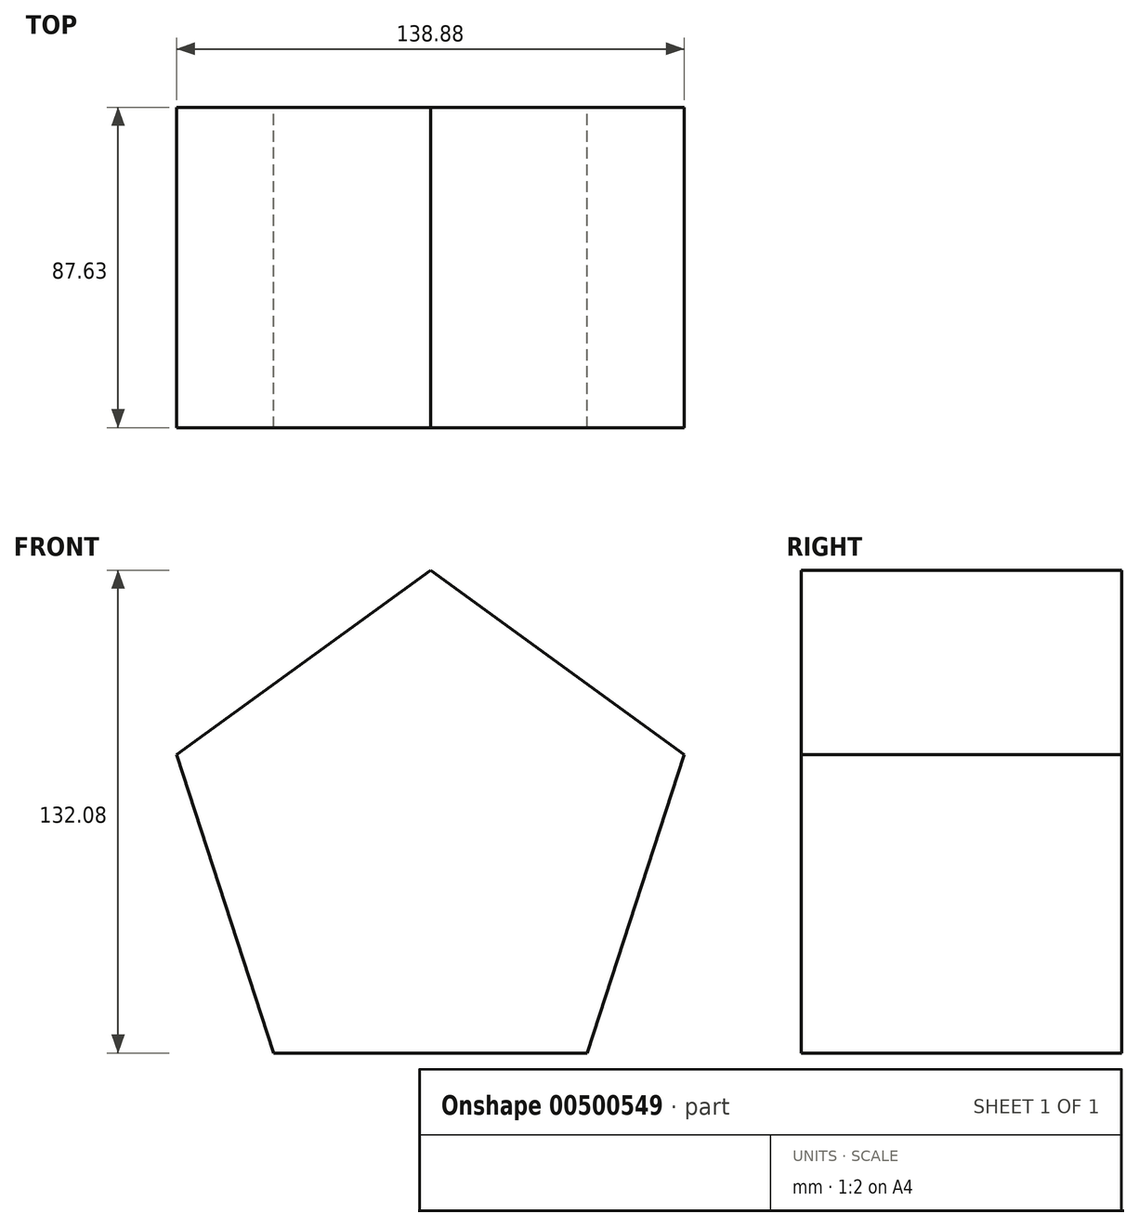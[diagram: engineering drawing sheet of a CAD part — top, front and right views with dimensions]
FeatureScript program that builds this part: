
annotation { "Feature Type Name" : "Feature", "Feature Type Description" : "" }
export const myFeature = defineFeature(function(context is Context, id is Id, definition is map)
    precondition{}
    {
        {
            var Q0;
            Q0=qCreatedBy(makeId("Front.planeOp"),FACE);
            var sketch = newSketch(context, id + "F0", { "sketchPlane" : qUnion([Q0])});
            skCircle(sketch, "E0.cCircle", {"center": v(0, 0) * mm, "radius": 73.01 * mm, "construction": true});
            skLineSegment(sketch, "E0.0", {"start": v(0, 73.01) * mm, "end": v(69.44, 22.56) * mm});
            skLineSegment(sketch, "E0.1", {"start": v(69.44, 22.56) * mm, "end": v(42.92, -59.07) * mm});
            skLineSegment(sketch, "E0.2", {"start": v(42.92, -59.07) * mm, "end": v(-42.92, -59.07) * mm});
            skLineSegment(sketch, "E0.3", {"start": v(-42.92, -59.07) * mm, "end": v(-69.44, 22.56) * mm});
            skLineSegment(sketch, "E0.4", {"start": v(-69.44, 22.56) * mm, "end": v(0, 73.01) * mm});
            skSolve(sketch);
        }
        {
            var Q0;
            Q0=makeQuery(id+"F0.imprint","IMPRINT",FACE,{"disambiguationData":[TD([[makeQuery(id+"F0.imprint","IMPRINT",EDGE,{"derivedFrom":sQuery(id+"F0.wireOp",EDGE,"E0.0")}),-1.0]])]});
            extrude(context, id + "F1", {"entities" : qUnion([Q0]), "depth" : 87.63 * mm});
        }
    });
